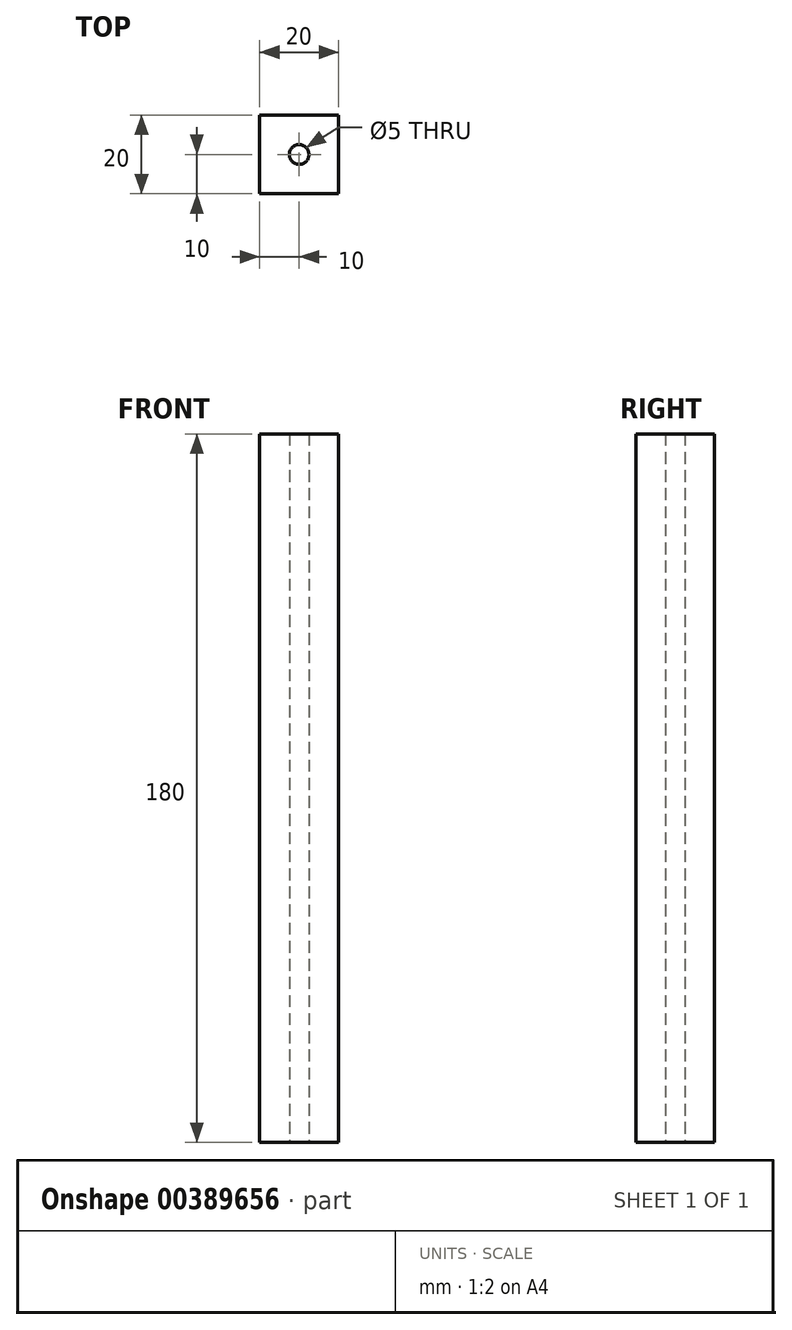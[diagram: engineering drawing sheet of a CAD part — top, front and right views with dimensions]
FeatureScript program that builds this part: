
annotation { "Feature Type Name" : "Feature", "Feature Type Description" : "" }
export const myFeature = defineFeature(function(context is Context, id is Id, definition is map)
    precondition{}
    {
        {
            var Q0;
            Q0=qCreatedBy(makeId("Top.planeOp"),FACE);
            var sketch = newSketch(context, id + "F0", { "sketchPlane" : qUnion([Q0])});
            skLineSegment(sketch, "E0.bottom", {"start": v(-10, 10) * mm, "end": v(10, 10) * mm});
            skLineSegment(sketch, "E0.top", {"start": v(-10, -10) * mm, "end": v(10, -10) * mm});
            skLineSegment(sketch, "E0.left", {"start": v(-10, 10) * mm, "end": v(-10, -10) * mm});
            skLineSegment(sketch, "E0.right", {"start": v(10, 10) * mm, "end": v(10, -10) * mm});
            skCircle(sketch, "E1", {"center": v(0, 0) * mm, "radius": 2.5 * mm});
            skSolve(sketch);
        }
        {
            var Q0;
            Q0=qSketchRegion(id+"F0",true);
            extrude(context, id + "F1", {"entities" : qUnion([Q0]), "depth" : 180 * mm});
        }
        {
            var Q0;
            Q0=makeQuery(id+"F1.opExtrude","SWEPT_FACE",FACE,{"disambiguationData":[OSD([sQuery(id+"F0.wireOp",EDGE,"E0.right")])]});
            var sketch = newSketch(context, id + "F2", { "sketchPlane" : qUnion([Q0])});
            skCircle(sketch, "E2", {"center": v(0, 10) * mm, "radius": 2.5 * mm});
            skSolve(sketch);
        }
    });
